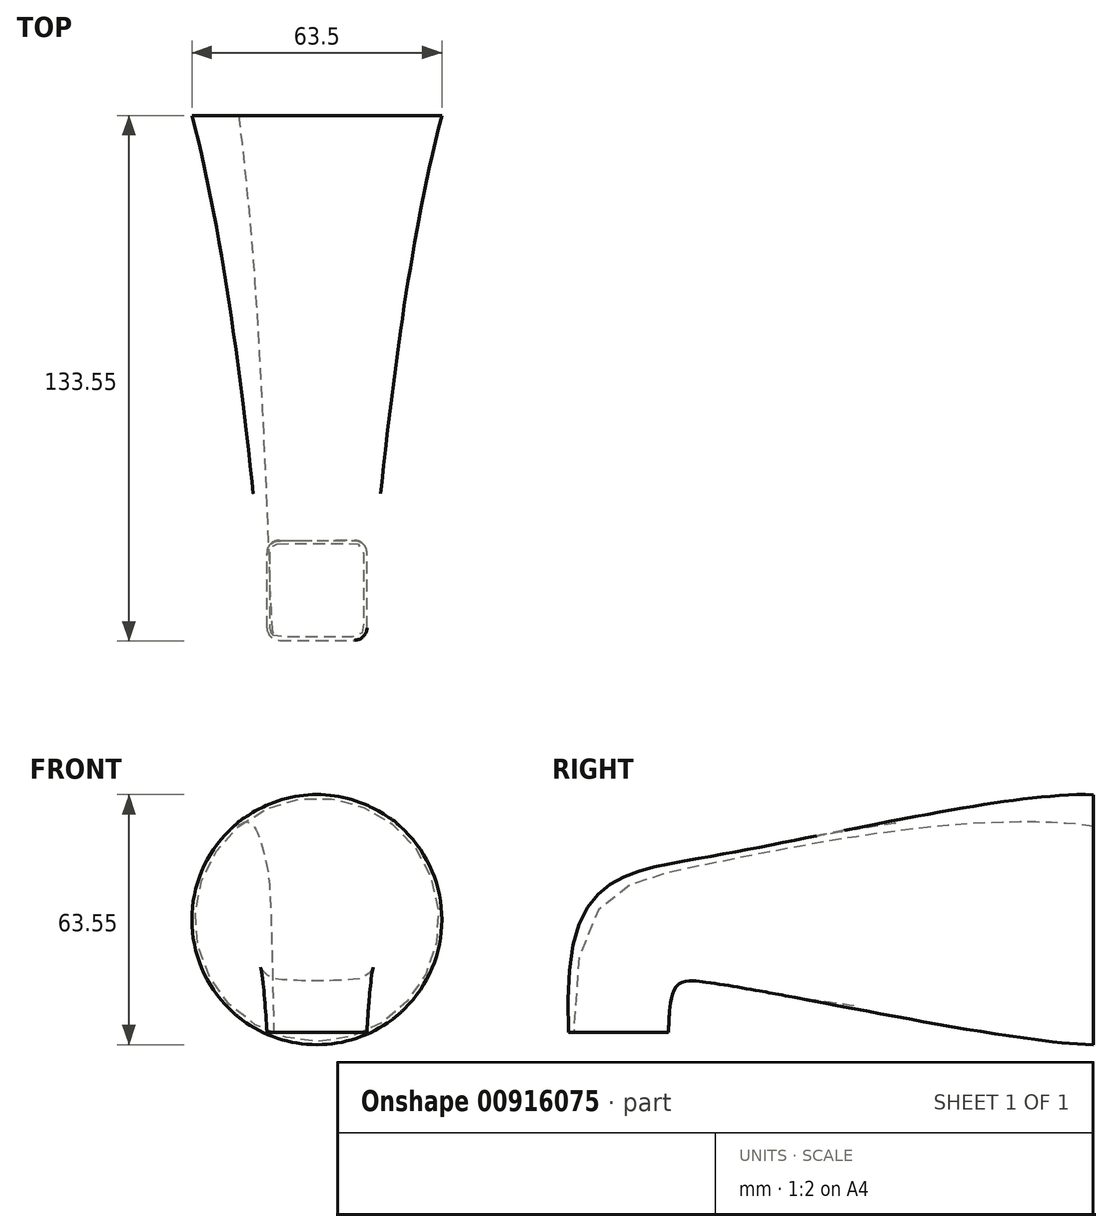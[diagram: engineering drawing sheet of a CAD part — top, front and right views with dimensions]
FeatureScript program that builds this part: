
annotation { "Feature Type Name" : "Feature", "Feature Type Description" : "" }
export const myFeature = defineFeature(function(context is Context, id is Id, definition is map)
    precondition{}
    {
        {
            var Q0;
            Q0=qCreatedBy(makeId("Right.planeOp"),FACE);
            var sketch = newSketch(context, id + "F0", { "sketchPlane" : qUnion([Q0])});
            skLineSegment(sketch, "E0", {"start": v(0, 0) * mm, "end": v(-98.43, 0) * mm});
            skArc(sketch, "E1", {"start": v(-98.43, 0) * mm, "mid": v(-114.14, -6.5) * mm, "end": v(-120.65, -22.23) * mm});
            skLineSegment(sketch, "E2", {"start": v(-120.65, -22.23) * mm, "end": v(-120.65, -28.58) * mm});
            skSolve(sketch);
        }
        {
            var Q0;
            Q0=qCreatedBy(makeId("Top.planeOp"),FACE);
            var Q1;
            Q1=sQuery(id+"F0.wireOp",VERTEX,"E2.end");
            cPlane(context, id + "F1", {"entities" : qUnion([Q0, Q1]), "cplaneType" : CPlaneType.PLANE_POINT, "offset" : 25.4 * mm, "width" : 152.4 * mm, "height" : 152.4 * mm});
        }
        {
            var Q0;
            Q0=qCreatedBy(id+"F1.planeOp",FACE);
            var sketch = newSketch(context, id + "F2", { "sketchPlane" : qUnion([Q0])});
            skLineSegment(sketch, "E3.bottom", {"start": v(-9.53, -133.35) * mm, "end": v(9.52, -133.35) * mm});
            skLineSegment(sketch, "E3.top", {"start": v(-9.53, -107.95) * mm, "end": v(9.52, -107.95) * mm});
            skLineSegment(sketch, "E3.left", {"start": v(-12.7, -130.18) * mm, "end": v(-12.7, -111.12) * mm});
            skLineSegment(sketch, "E3.right", {"start": v(12.7, -130.18) * mm, "end": v(12.7, -111.12) * mm});
            skPoint(sketch, "E3.middle", {"position": v(0, -120.65) * mm});
            skPoint(sketch, "E4.visualSharp", {"position": v(-12.7, -107.95) * mm});
            skArc(sketch, "E4.filletArc", {"start": v(-9.53, -107.95) * mm, "mid": v(-11.77, -108.88) * mm, "end": v(-12.7, -111.12) * mm});
            skPoint(sketch, "E5.visualSharp", {"position": v(-12.7, -133.35) * mm});
            skArc(sketch, "E5.filletArc", {"start": v(-12.7, -130.18) * mm, "mid": v(-11.77, -132.42) * mm, "end": v(-9.53, -133.35) * mm});
            skPoint(sketch, "E6.visualSharp", {"position": v(12.7, -133.35) * mm});
            skArc(sketch, "E6.filletArc", {"start": v(9.52, -133.35) * mm, "mid": v(11.77, -132.42) * mm, "end": v(12.7, -130.18) * mm});
            skPoint(sketch, "E7.visualSharp", {"position": v(12.7, -107.95) * mm});
            skArc(sketch, "E7.filletArc", {"start": v(12.7, -111.12) * mm, "mid": v(11.77, -108.88) * mm, "end": v(9.52, -107.95) * mm});
            skSolve(sketch);
        }
        {
            var Q0;
            Q0=qCreatedBy(makeId("Front.planeOp"),FACE);
            var sketch = newSketch(context, id + "F3", { "sketchPlane" : qUnion([Q0])});
            skLineSegment(sketch, "E8", {"start": v(0, 0) * mm, "end": v(19.05, 25.4) * mm, "construction": true});
            skPoint(sketch, "E9.center", {"position": v(0, 0) * mm});
            skLineSegment(sketch, "E10", {"start": v(0, 0) * mm, "end": v(22.23, 22.67) * mm, "construction": true});
            skLineSegment(sketch, "E11.MirrorCS", {"start": v(0, 0) * mm, "end": v(22.23, -22.67) * mm, "construction": true});
            skLineSegment(sketch, "E12.MirrorCS", {"start": v(0, 0) * mm, "end": v(19.05, -25.4) * mm, "construction": true});
            skLineSegment(sketch, "E13.MirrorCS", {"start": v(0, 0) * mm, "end": v(-19.05, 25.4) * mm, "construction": true});
            skLineSegment(sketch, "E14.MirrorCS", {"start": v(0, 0) * mm, "end": v(-22.23, 22.67) * mm, "construction": true});
            skLineSegment(sketch, "E15.MirrorCS", {"start": v(0, 0) * mm, "end": v(-22.23, -22.67) * mm, "construction": true});
            skLineSegment(sketch, "E16.MirrorCS", {"start": v(0, 0) * mm, "end": v(-19.05, -25.4) * mm, "construction": true});
            skArc(sketch, "E17", {"start": v(-22.23, 22.67) * mm, "mid": v(-31.75, 0) * mm, "end": v(-22.22, -22.67) * mm});
            skArc(sketch, "E18", {"start": v(-19.05, 25.4) * mm, "mid": v(-20.68, 24.09) * mm, "end": v(-22.23, 22.67) * mm});
            skArc(sketch, "E19", {"start": v(19.05, 25.4) * mm, "mid": v(0, 31.75) * mm, "end": v(-19.05, 25.4) * mm});
            skArc(sketch, "E20", {"start": v(22.22, 22.67) * mm, "mid": v(20.68, 24.09) * mm, "end": v(19.05, 25.4) * mm});
            skArc(sketch, "E21", {"start": v(22.22, -22.67) * mm, "mid": v(31.75, 0) * mm, "end": v(22.23, 22.67) * mm});
            skArc(sketch, "E22", {"start": v(19.05, -25.4) * mm, "mid": v(20.68, -24.09) * mm, "end": v(22.22, -22.67) * mm});
            skArc(sketch, "E23", {"start": v(-19.05, -25.4) * mm, "mid": v(0, -31.75) * mm, "end": v(19.05, -25.4) * mm});
            skArc(sketch, "E24", {"start": v(-22.22, -22.67) * mm, "mid": v(-20.68, -24.09) * mm, "end": v(-19.05, -25.4) * mm});
            skSolve(sketch);
        }
        {
            var Q0;
            Q0=qCreatedBy(makeId("Front.planeOp"),FACE);
            var Q1;
            Q1=sQuery(id+"F0.wireOp",VERTEX,"E0.end");
            cPlane(context, id + "F4", {"entities" : qUnion([Q0, Q1]), "cplaneType" : CPlaneType.PLANE_POINT, "offset" : 25.4 * mm, "width" : 152.4 * mm, "height" : 152.4 * mm});
        }
        {
            var Q0;
            Q0=qCreatedBy(id+"F4.planeOp",FACE);
            var sketch = newSketch(context, id + "F5", { "sketchPlane" : qUnion([Q0])});
            skLineSegment(sketch, "E25.bottom", {"start": v(9.52, 15.88) * mm, "end": v(-9.52, 15.88) * mm});
            skLineSegment(sketch, "E25.top", {"start": v(9.52, -15.88) * mm, "end": v(-9.52, -15.88) * mm});
            skLineSegment(sketch, "E25.left", {"start": v(15.88, 9.52) * mm, "end": v(15.88, -9.52) * mm});
            skLineSegment(sketch, "E25.right", {"start": v(-15.88, 9.52) * mm, "end": v(-15.88, -9.52) * mm});
            skPoint(sketch, "E25.middle", {"position": v(0, 0) * mm});
            skPoint(sketch, "E26.visualSharp", {"position": v(-15.88, 15.88) * mm});
            skArc(sketch, "E26.filletArc", {"start": v(-9.52, 15.88) * mm, "mid": v(-14.02, 14.02) * mm, "end": v(-15.88, 9.52) * mm});
            skPoint(sketch, "E27.visualSharp", {"position": v(15.88, 15.88) * mm});
            skArc(sketch, "E27.filletArc", {"start": v(15.88, 9.52) * mm, "mid": v(14.02, 14.02) * mm, "end": v(9.52, 15.88) * mm});
            skPoint(sketch, "E28.visualSharp", {"position": v(15.88, -15.88) * mm});
            skArc(sketch, "E28.filletArc", {"start": v(9.52, -15.88) * mm, "mid": v(14.02, -14.02) * mm, "end": v(15.88, -9.52) * mm});
            skPoint(sketch, "E29.visualSharp", {"position": v(-15.88, -15.88) * mm});
            skArc(sketch, "E29.filletArc", {"start": v(-15.88, -9.52) * mm, "mid": v(-14.02, -14.02) * mm, "end": v(-9.52, -15.88) * mm});
            skSolve(sketch);
        }
        {
            var Q0;
            Q0=qCreatedBy(makeId("Right.planeOp"),FACE);
            var sketch = newSketch(context, id + "F6", { "sketchPlane" : qUnion([Q0])});
            skFitSpline(sketch, "E30", {"points": [v(0, 31.75) * mm, v(-98.43, 15.88) * mm, v(-133.35, -28.58) * mm], "startDerivative": vector(-109.65, 4.5) * mm, "endDerivative": vector(14.3, -277.72) * mm});
            skFitSpline(sketch, "E31", {"points": [v(0, -31.75) * mm, v(-98.43, -15.88) * mm, v(-107.95, -28.58) * mm], "startDerivative": vector(-91.55, 1.45) * mm, "endDerivative": vector(-2.39, -137.3) * mm});
            skSolve(sketch);
        }
        {
            var Q0;
            Q0 = qSketchRegion(id + "F3", true);
            var Q1;
            Q1 = qSketchRegion(id + "F5", true);
            var Q2;
            Q2 = qSketchRegion(id + "F2", true);
            var Q3;
            Q3=sQuery(id+"F6.wireOp",EDGE,"E30");
            var Q4;
            Q4=sQuery(id+"F6.wireOp",EDGE,"E31");
            loft(context, id + "F7", {"addGuides" : true, "sheetProfilesArray" : [{ "sheetProfileEntities" : qUnion([Q0]) }, { "sheetProfileEntities" : qUnion([Q1]) }, { "sheetProfileEntities" : qUnion([Q2]) }], "guidesArray" : [{ "guideEntities" : qUnion([Q3]), "guideDerivativeType" : LoftGuideDerivativeType.DEFAULT, "guideDerivativeMagnitude" : 1 }, { "guideEntities" : qUnion([Q4]), "guideDerivativeType" : LoftGuideDerivativeType.DEFAULT, "guideDerivativeMagnitude" : 1 }]});
        }
        {
            var Q0;
            Q0=makeQuery(id+"F7.opLoft","CAP_FACE",FACE,{"disambiguationData":[OSD([makeQuery(id+"F3.imprint","IMPRINT",FACE,{"disambiguationData":[TD([[makeQuery(id+"F3.imprint","IMPRINT",EDGE,{"derivedFrom":sQuery(id+"F3.wireOp",EDGE,"E17")}),1.0]])]})])],"isStart":true});
            var Q1;
            Q1=makeQuery(id+"F7.opLoft","CAP_FACE",FACE,{"disambiguationData":[OSD([makeQuery(id+"F2.imprint","IMPRINT",FACE,{"disambiguationData":[TD([[makeQuery(id+"F2.imprint","IMPRINT",EDGE,{"derivedFrom":sQuery(id+"F2.wireOp",EDGE,"E3.bottom")}),1.0]])]})])],"isStart":true});
            shell(context, id + "F8", {"entities" : qUnion([Q0, Q1]), "thickness" : 0.8 * mm});
        }
    });
